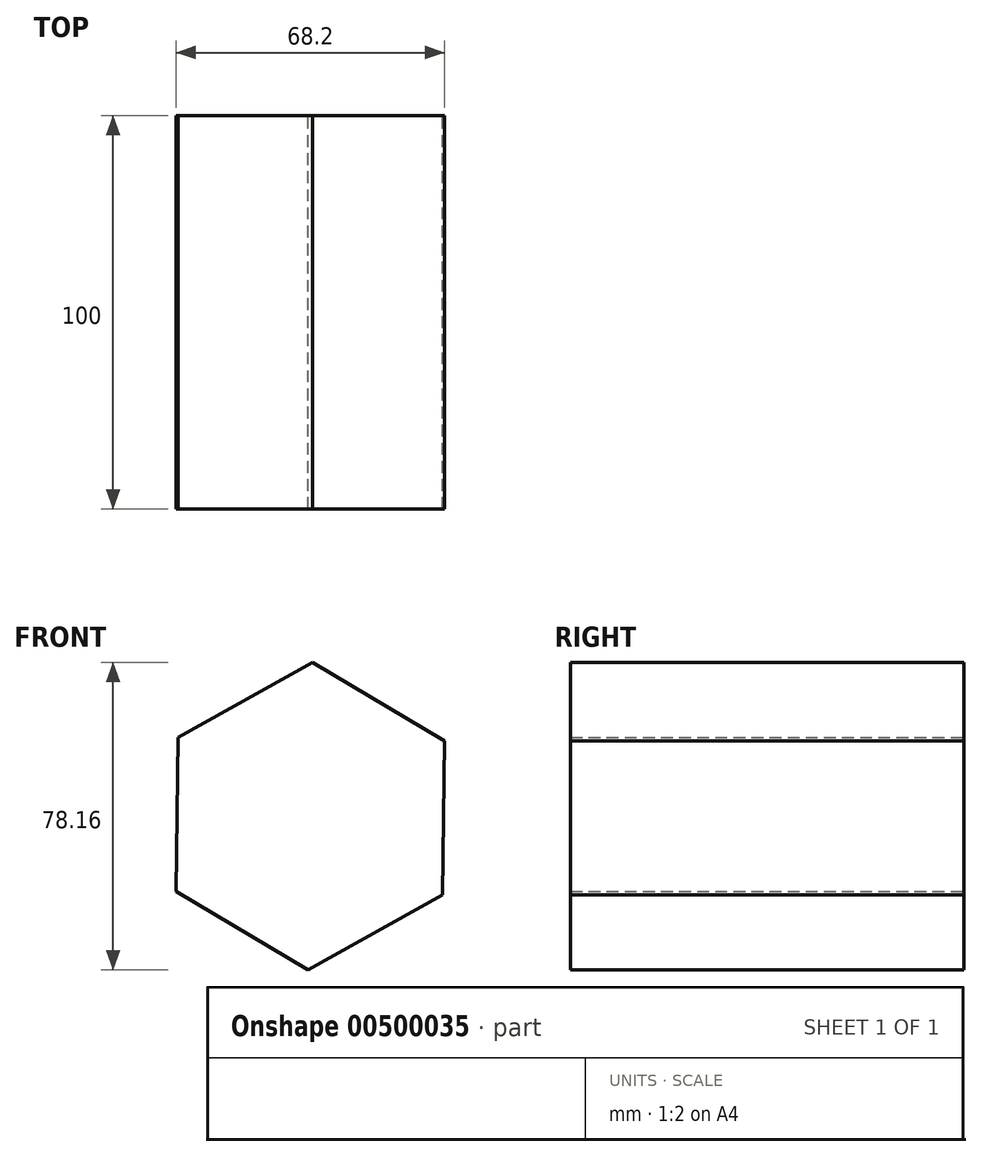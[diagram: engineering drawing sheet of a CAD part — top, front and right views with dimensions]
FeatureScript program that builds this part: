
annotation { "Feature Type Name" : "Feature", "Feature Type Description" : "" }
export const myFeature = defineFeature(function(context is Context, id is Id, definition is map)
    precondition{}
    {
        {
            var Q0;
            Q0=qCreatedBy(makeId("Front.planeOp"),FACE);
            var sketch = newSketch(context, id + "F0", { "sketchPlane" : qUnion([Q0])});
            skCircle(sketch, "E0.cCircle", {"center": v(0, 0) * mm, "radius": 39.08 * mm, "construction": true});
            skLineSegment(sketch, "E0.0", {"start": v(34.1, 19.1) * mm, "end": v(33.59, -19.99) * mm});
            skLineSegment(sketch, "E0.1", {"start": v(33.59, -19.99) * mm, "end": v(-0.52, -39.08) * mm});
            skLineSegment(sketch, "E0.2", {"start": v(-0.52, -39.08) * mm, "end": v(-34.1, -19.1) * mm});
            skLineSegment(sketch, "E0.3", {"start": v(-34.1, -19.1) * mm, "end": v(-33.59, 19.99) * mm});
            skLineSegment(sketch, "E0.4", {"start": v(-33.59, 19.99) * mm, "end": v(0.52, 39.08) * mm});
            skLineSegment(sketch, "E0.5", {"start": v(0.52, 39.08) * mm, "end": v(34.1, 19.1) * mm});
            skSolve(sketch);
        }
        {
            var Q0;
            Q0 = qSketchRegion(id + "F0", true);
            extrude(context, id + "F1", {"entities" : qUnion([Q0]), "endBound" : BoundingType.SYMMETRIC, "depth" : 100 * mm});
        }
    });
